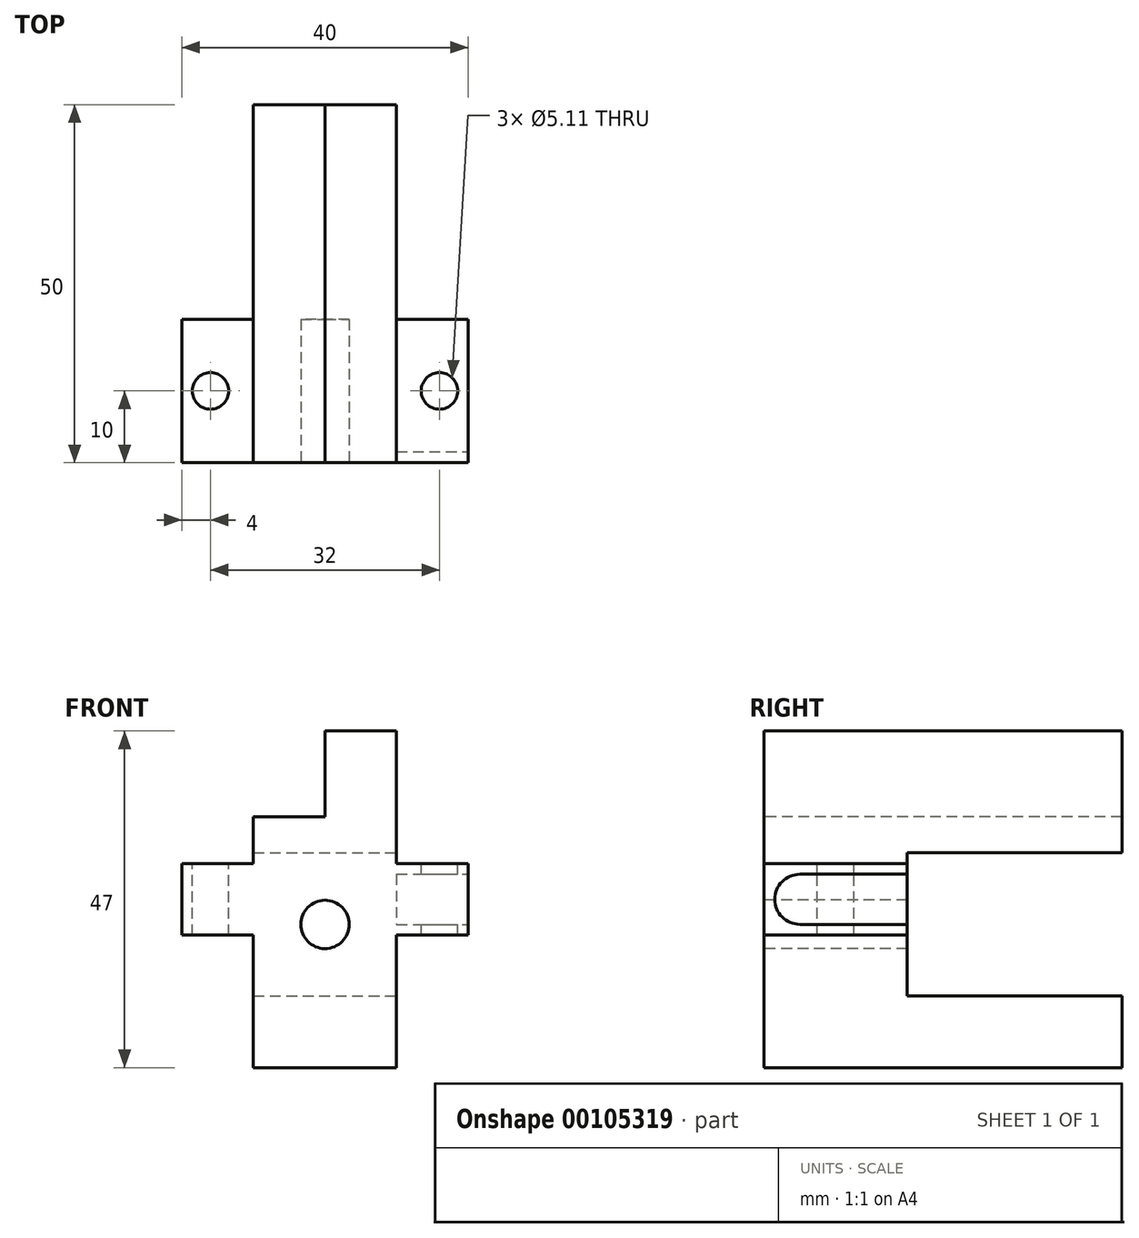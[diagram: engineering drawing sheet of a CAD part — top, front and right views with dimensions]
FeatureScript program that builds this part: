
annotation { "Feature Type Name" : "Feature", "Feature Type Description" : "" }
export const myFeature = defineFeature(function(context is Context, id is Id, definition is map)
    precondition{}
    {
        {
            var Q0;
            Q0=qCreatedBy(makeId("Front.planeOp"),FACE);
            var sketch = newSketch(context, id + "F0", { "sketchPlane" : qUnion([Q0])});
            skLineSegment(sketch, "E0", {"start": v(0, 26.17) * mm, "end": v(0, -25.07) * mm, "construction": true});
            skPoint(sketch, "E1", {"position": v(0, -20) * mm});
            skLineSegment(sketch, "E2", {"start": v(-31.95, 0) * mm, "end": v(29.47, 0) * mm, "construction": true});
            skPoint(sketch, "E3", {"position": v(0, 0) * mm});
            skLineSegment(sketch, "E4.top", {"start": v(0, 27) * mm, "end": v(10, 27) * mm});
            skLineSegment(sketch, "E4.left", {"start": v(0, 15) * mm, "end": v(0, 27) * mm});
            skLineSegment(sketch, "E4.right", {"start": v(10, 8.5) * mm, "end": v(10, 27) * mm});
            skLineSegment(sketch, "E5", {"start": v(10, 8.5) * mm, "end": v(20, 8.5) * mm});
            skLineSegment(sketch, "E6", {"start": v(-10, 15) * mm, "end": v(-10, 8.5) * mm});
            skLineSegment(sketch, "E7", {"start": v(-10, 8.5) * mm, "end": v(-20, 8.5) * mm});
            skLineSegment(sketch, "E8", {"start": v(-20, -1.5) * mm, "end": v(-10, -1.5) * mm});
            skLineSegment(sketch, "E9", {"start": v(-10, -1.5) * mm, "end": v(-10, -20) * mm});
            skLineSegment(sketch, "E10", {"start": v(10, -20) * mm, "end": v(10, -1.5) * mm});
            skLineSegment(sketch, "E11", {"start": v(10, -1.5) * mm, "end": v(20, -1.5) * mm});
            skLineSegment(sketch, "E12", {"start": v(-20, 8.5) * mm, "end": v(-20, -1.5) * mm});
            skLineSegment(sketch, "E13", {"start": v(-10, -20) * mm, "end": v(10, -20) * mm});
            skLineSegment(sketch, "E14", {"start": v(20, 8.5) * mm, "end": v(20, -1.5) * mm});
            skLineSegment(sketch, "E15", {"start": v(-10, 15) * mm, "end": v(0, 15) * mm});
            skLineSegment(sketch, "E16", {"start": v(-27.25, 3.5) * mm, "end": v(27.2, 3.5) * mm, "construction": true});
            skPoint(sketch, "E17", {"position": v(20, 3.5) * mm});
            skSolve(sketch);
        }
        {
            var Q0;
            Q0=makeQuery(id+"F0.imprint","IMPRINT",FACE,{"disambiguationData":[TD([[makeQuery(id+"F0.imprint","IMPRINT",EDGE,{"derivedFrom":sQuery(id+"F0.wireOp",EDGE,"FzGxt0yV-aUSP-FFbB-Mpb3-oRu5jpN99Y81.bottom")}),1.0]])]});
            var Q1;
            Q1=makeQuery(id+"F0.imprint","IMPRINT",FACE,{"disambiguationData":[TD([[makeQuery(id+"F0.imprint","IMPRINT",EDGE,{"derivedFrom":sQuery(id+"F0.wireOp",EDGE,"E4.top")}),-1.0]])]});
            extrude(context, id + "F1", {"entities" : qUnion([Q0, Q1]), "endBound" : BoundingType.SYMMETRIC, "oppositeDirection" : true, "depth" : 50 * mm});
        }
        {
            var Q0;
            Q0=makeQuery(id+"F1.opExtrude","CAP_FACE",FACE,{"disambiguationData":[OSD([sQuery(id+"F0.wireOp",EDGE,"E4.top"),sQuery(id+"F0.wireOp",EDGE,"E4.left"),sQuery(id+"F0.wireOp",EDGE,"E4.right"),sQuery(id+"F0.wireOp",EDGE,"E5"),sQuery(id+"F0.wireOp",EDGE,"E6"),sQuery(id+"F0.wireOp",EDGE,"E7"),sQuery(id+"F0.wireOp",EDGE,"E8"),sQuery(id+"F0.wireOp",EDGE,"E9"),sQuery(id+"F0.wireOp",EDGE,"E10"),sQuery(id+"F0.wireOp",EDGE,"E11"),sQuery(id+"F0.wireOp",EDGE,"E12"),sQuery(id+"F0.wireOp",EDGE,"E13"),sQuery(id+"F0.wireOp",EDGE,"E14"),sQuery(id+"F0.wireOp",EDGE,"E15")])],"isStart":true});
            var sketch = newSketch(context, id + "F2", { "sketchPlane" : qUnion([Q0])});
            skPoint(sketch, "E18", {"position": v(0, 0) * mm});
            skSolve(sketch);
        }
        {
            var Q0;
            Q0=sQuery(id+"F2.wireOp",VERTEX,"E18");
            var Q1;
            Q1=makeQuery(id+"F1.opExtrude","SWEPT_BODY",BODY,{"disambiguationData":[OSD([sQuery(id+"F0.wireOp",EDGE,"E4.top"),sQuery(id+"F0.wireOp",EDGE,"E4.left"),sQuery(id+"F0.wireOp",EDGE,"E4.right"),sQuery(id+"F0.wireOp",EDGE,"E5"),sQuery(id+"F0.wireOp",EDGE,"E6"),sQuery(id+"F0.wireOp",EDGE,"E7"),sQuery(id+"F0.wireOp",EDGE,"E8"),sQuery(id+"F0.wireOp",EDGE,"E9"),sQuery(id+"F0.wireOp",EDGE,"E10"),sQuery(id+"F0.wireOp",EDGE,"E11"),sQuery(id+"F0.wireOp",EDGE,"E12"),sQuery(id+"F0.wireOp",EDGE,"E13"),sQuery(id+"F0.wireOp",EDGE,"E14"),sQuery(id+"F0.wireOp",EDGE,"E15")])]});
            hole(context, id + "F3", {"style" : HoleStyle.SIMPLE, "endStyle" : HoleEndStyle.THROUGH, "standardTappedOrClearance" : lookupTablePath({ "standard" : "ANSI", "fit" : "Normal (ASME)", "size" : "1/4", "type" : "Clearance" }), "standardBlindInLast" : lookupTablePath({ "fit" : "Free", "standard" : "ANSI", "size" : "1/4", "type" : "Clearance" }), "holeDiameter" : 6.76 * mm, "locations" : qUnion([Q0]), "scope" : qUnion([Q1]), "isTappedThrough" : true});
        }
        {
            var Q0;
            Q0=makeQuery(id+"F1.opExtrude","SWEPT_FACE",FACE,{"disambiguationData":[OSD([sQuery(id+"F0.wireOp",EDGE,"E14")])]});
            var sketch = newSketch(context, id + "F4", { "sketchPlane" : qUnion([Q0])});
            skLineSegment(sketch, "E19.bottom", {"start": v(-5, 10) * mm, "end": v(64.75, 10) * mm});
            skLineSegment(sketch, "E19.top", {"start": v(-5, -10) * mm, "end": v(64.75, -10) * mm});
            skLineSegment(sketch, "E19.left", {"start": v(-5, 10) * mm, "end": v(-5, -10) * mm});
            skLineSegment(sketch, "E19.right", {"start": v(64.75, 10) * mm, "end": v(64.75, -10) * mm});
            skLineSegment(sketch, "E20", {"start": v(-18.92, 0) * mm, "end": v(66.02, 0) * mm, "construction": true});
            skPoint(sketch, "E21", {"position": v(-5, 0) * mm});
            skSolve(sketch);
        }
        {
            var Q0;
            Q0 = qSketchRegion(id + "F4", true);
            extrude(context, id + "F5", {"entities" : qUnion([Q0]), "operationType" : NewBodyOperationType.REMOVE, "endBound" : BoundingType.THROUGH_ALL, "oppositeDirection" : true, "depth" : 25 * mm});
        }
        {
            var Q0;
            Q0=makeQuery(id+"F1.opExtrude","SWEPT_FACE",FACE,{"disambiguationData":[OSD([sQuery(id+"F0.wireOp",EDGE,"E14")])]});
            var sketch = newSketch(context, id + "F6", { "sketchPlane" : qUnion([Q0])});
            skLineSegment(sketch, "E22", {"start": v(-60.97, 0) * mm, "end": v(57.79, 0) * mm, "construction": true});
            skLineSegment(sketch, "E23", {"start": v(0, 40.74) * mm, "end": v(0, -43.05) * mm, "construction": true});
            skLineSegment(sketch, "E24.bottom", {"start": v(-20, 0) * mm, "end": v(-5, 0) * mm});
            skLineSegment(sketch, "E24.top", {"start": v(-20, 7) * mm, "end": v(-5, 7) * mm});
            skArc(sketch, "E25", {"start": v(-20, 7) * mm, "mid": v(-23.5, 3.5) * mm, "end": v(-20, 0) * mm});
            skSolve(sketch);
        }
        {
            var Q0;
            Q0=makeQuery(id+"F6.imprint","IMPRINT",FACE,{"disambiguationData":[TD([[makeQuery(id+"F6.imprint","IMPRINT",EDGE,{"derivedFrom":sQuery(id+"F6.wireOp",EDGE,"E24.bottom")}),1.0]])]});
            extrude(context, id + "F7", {"entities" : qUnion([Q0]), "operationType" : NewBodyOperationType.REMOVE, "oppositeDirection" : true, "depth" : 10 * mm});
        }
        {
            var Q0;
            Q0=makeQuery(id+"F1.opExtrude","SWEPT_FACE",FACE,{"disambiguationData":[OSD([sQuery(id+"F0.wireOp",EDGE,"E5")])]});
            var sketch = newSketch(context, id + "F8", { "sketchPlane" : qUnion([Q0])});
            skLineSegment(sketch, "E26", {"start": v(-40.22, -15) * mm, "end": v(46.74, -15) * mm, "construction": true});
            skPoint(sketch, "E27", {"position": v(16, -15) * mm});
            skPoint(sketch, "E28.MirrorP", {"position": v(-16, -15) * mm});
            skLineSegment(sketch, "E29", {"start": v(0, -33.54) * mm, "end": v(0, 11.74) * mm, "construction": true});
            skSolve(sketch);
        }
        {
            var Q0;
            Q0=sQuery(id+"F8.wireOp",VERTEX,"E27");
            var Q1;
            Q1=sQuery(id+"F8.wireOp",VERTEX,"E28.MirrorP");
            var Q2;
            Q2=makeQuery(id+"F1.opExtrude","SWEPT_BODY",BODY,{"disambiguationData":[OSD([sQuery(id+"F0.wireOp",EDGE,"E4.top"),sQuery(id+"F0.wireOp",EDGE,"E4.left"),sQuery(id+"F0.wireOp",EDGE,"E4.right"),sQuery(id+"F0.wireOp",EDGE,"E5"),sQuery(id+"F0.wireOp",EDGE,"E6"),sQuery(id+"F0.wireOp",EDGE,"E7"),sQuery(id+"F0.wireOp",EDGE,"E8"),sQuery(id+"F0.wireOp",EDGE,"E9"),sQuery(id+"F0.wireOp",EDGE,"E10"),sQuery(id+"F0.wireOp",EDGE,"E11"),sQuery(id+"F0.wireOp",EDGE,"E12"),sQuery(id+"F0.wireOp",EDGE,"E13"),sQuery(id+"F0.wireOp",EDGE,"E14"),sQuery(id+"F0.wireOp",EDGE,"E15")])]});
            hole(context, id + "F9", {"style" : HoleStyle.SIMPLE, "endStyle" : HoleEndStyle.THROUGH, "standardTappedOrClearance" : lookupTablePath({ "standard" : "ANSI", "fit" : "Normal (ASME)", "size" : "#10", "type" : "Clearance" }), "standardBlindInLast" : lookupTablePath({ "fit" : "Free", "standard" : "ANSI", "size" : "#10", "type" : "Clearance" }), "holeDiameter" : 5.1 * mm, "locations" : qUnion([Q0, Q1]), "scope" : qUnion([Q2]), "isTappedThrough" : true});
        }
    });
